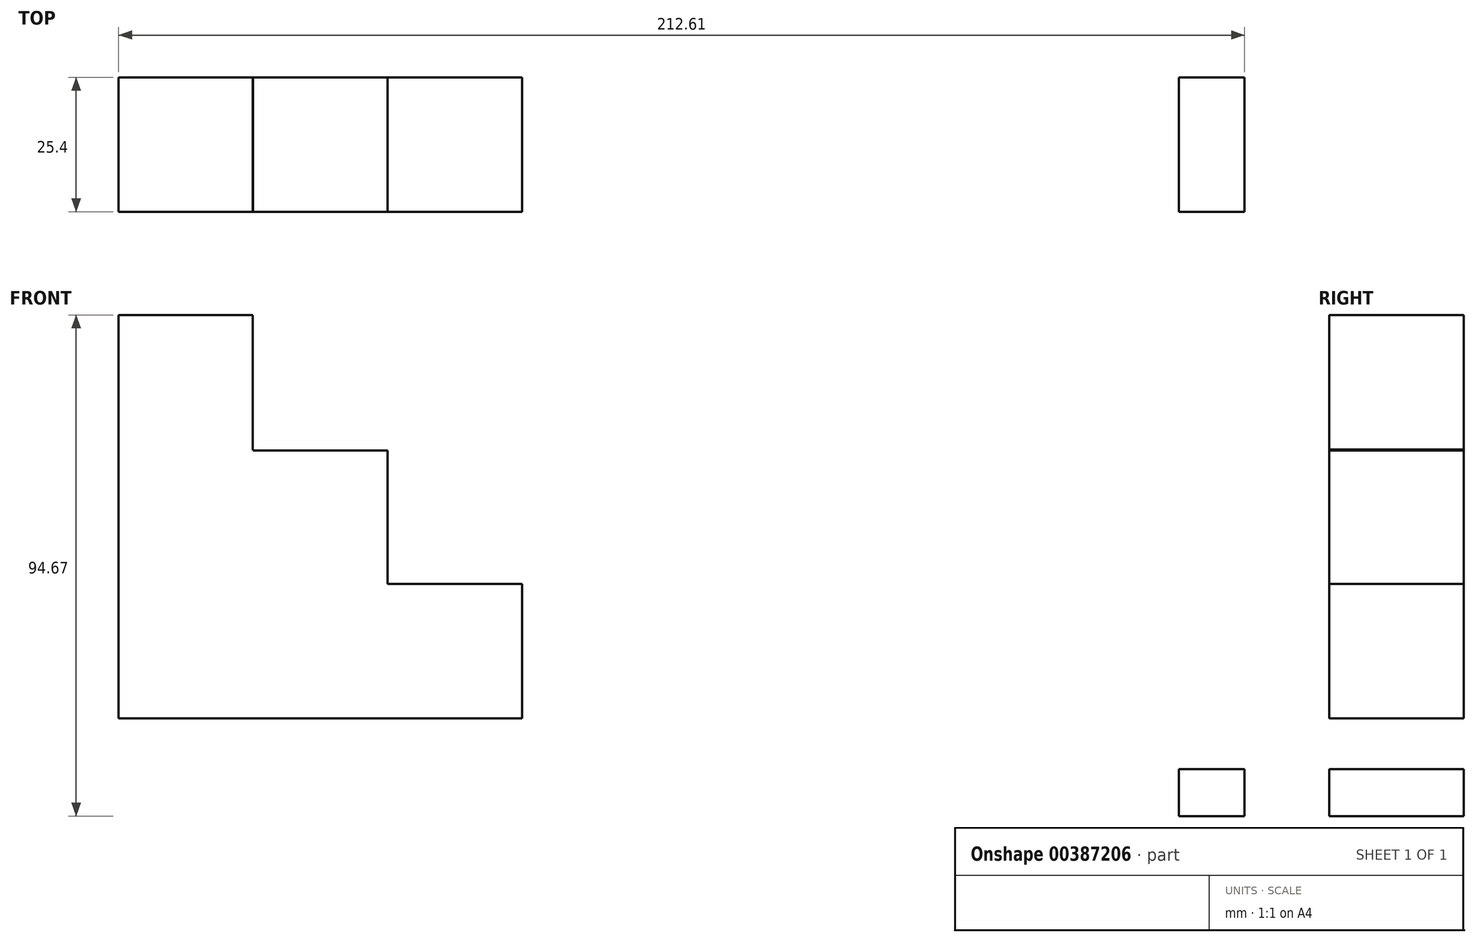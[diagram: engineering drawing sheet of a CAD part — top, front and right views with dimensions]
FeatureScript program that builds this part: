
annotation { "Feature Type Name" : "Feature", "Feature Type Description" : "" }
export const myFeature = defineFeature(function(context is Context, id is Id, definition is map)
    precondition{}
    {
        {
            var Q0;
            Q0=qCreatedBy(makeId("Front.planeOp"),FACE);
            var sketch = newSketch(context, id + "F0", { "sketchPlane" : qUnion([Q0])});
            skLineSegment(sketch, "E0.bottom", {"start": v(0, 0) * mm, "end": v(25.4, 0) * mm});
            skLineSegment(sketch, "E0.top", {"start": v(0, 25.4) * mm, "end": v(25.4, 25.4) * mm});
            skLineSegment(sketch, "E0.left", {"start": v(0, 0) * mm, "end": v(0, 25.4) * mm});
            skLineSegment(sketch, "E0.right", {"start": v(25.4, 0) * mm, "end": v(25.4, 25.4) * mm});
            skLineSegment(sketch, "E1.bottom", {"start": v(0, 25.4) * mm, "end": v(-25.4, 25.4) * mm});
            skLineSegment(sketch, "E1.top", {"start": v(0, 0) * mm, "end": v(-25.4, 0) * mm});
            skLineSegment(sketch, "E1.left", {"start": v(0, 25.4) * mm, "end": v(0, 0) * mm});
            skLineSegment(sketch, "E1.right", {"start": v(-25.4, 25.4) * mm, "end": v(-25.4, 0) * mm});
            skLineSegment(sketch, "E2.bottom", {"start": v(149.38, -9.6) * mm, "end": v(161.81, -9.6) * mm});
            skLineSegment(sketch, "E2.top", {"start": v(149.38, -18.47) * mm, "end": v(161.81, -18.47) * mm});
            skLineSegment(sketch, "E2.left", {"start": v(149.38, -9.6) * mm, "end": v(149.38, -18.47) * mm});
            skLineSegment(sketch, "E2.right", {"start": v(161.81, -9.6) * mm, "end": v(161.81, -18.47) * mm});
            skLineSegment(sketch, "E3.bottom", {"start": v(161.81, -18.47) * mm, "end": v(155.6, -18.47) * mm});
            skLineSegment(sketch, "E3.top", {"start": v(161.81, -9.6) * mm, "end": v(155.6, -9.6) * mm});
            skLineSegment(sketch, "E3.left", {"start": v(161.81, -18.47) * mm, "end": v(161.81, -9.6) * mm});
            skLineSegment(sketch, "E3.right", {"start": v(155.6, -18.47) * mm, "end": v(155.6, -9.6) * mm});
            skLineSegment(sketch, "E4.bottom", {"start": v(-25.4, 25.4) * mm, "end": v(-50.8, 25.4) * mm});
            skLineSegment(sketch, "E4.top", {"start": v(-25.4, 50.8) * mm, "end": v(-50.8, 50.8) * mm});
            skLineSegment(sketch, "E4.left", {"start": v(-25.4, 25.4) * mm, "end": v(-25.4, 50.8) * mm});
            skLineSegment(sketch, "E4.right", {"start": v(-50.8, 25.4) * mm, "end": v(-50.8, 50.8) * mm});
            skLineSegment(sketch, "E5.bottom", {"start": v(-50.8, 50.8) * mm, "end": v(-25.45, 50.8) * mm});
            skLineSegment(sketch, "E5.top", {"start": v(-50.8, 76.2) * mm, "end": v(-25.45, 76.2) * mm});
            skLineSegment(sketch, "E5.left", {"start": v(-50.8, 50.8) * mm, "end": v(-50.8, 76.2) * mm});
            skLineSegment(sketch, "E5.right", {"start": v(-25.45, 50.8) * mm, "end": v(-25.45, 76.2) * mm});
            skLineSegment(sketch, "E6.bottom", {"start": v(-50.8, 25.4) * mm, "end": v(-25.4, 25.4) * mm});
            skLineSegment(sketch, "E6.top", {"start": v(-50.8, 0) * mm, "end": v(-25.4, 0) * mm});
            skLineSegment(sketch, "E6.left", {"start": v(-50.8, 25.4) * mm, "end": v(-50.8, 0) * mm});
            skLineSegment(sketch, "E7.bottom", {"start": v(-25.4, 25.4) * mm, "end": v(0, 25.4) * mm});
            skLineSegment(sketch, "E7.top", {"start": v(-25.4, 50.62) * mm, "end": v(0, 50.62) * mm});
            skLineSegment(sketch, "E7.left", {"start": v(-25.4, 25.4) * mm, "end": v(-25.4, 50.62) * mm});
            skLineSegment(sketch, "E7.right", {"start": v(0, 25.4) * mm, "end": v(0, 50.62) * mm});
            skSolve(sketch);
        }
        {
            var Q0;
            Q0 = qSketchRegion(id + "F0", true);
            extrude(context, id + "F1", {"entities" : qUnion([Q0]), "depth" : 25.4 * mm});
        }
    });
